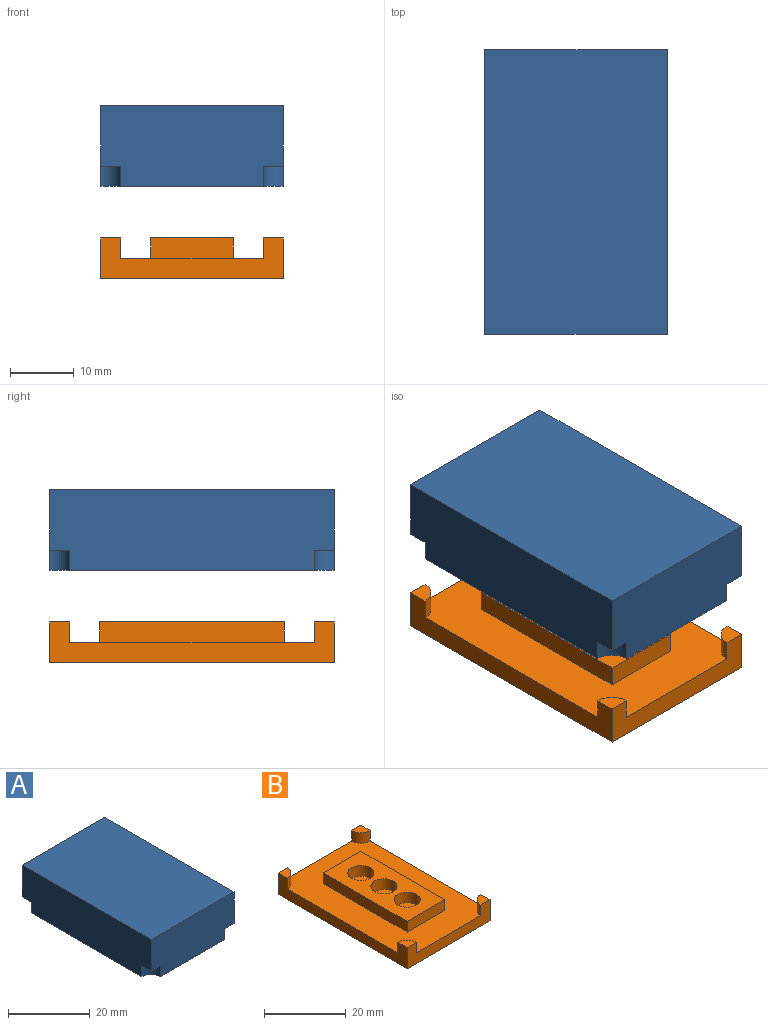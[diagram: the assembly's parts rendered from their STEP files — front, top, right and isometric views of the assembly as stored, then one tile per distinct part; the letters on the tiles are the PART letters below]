
ASSEMBLY  parts=2 mates=1
PART A: 55 faces, bbox 28.7x44.7x12.7 mm
  f0: plane 44.7x28.7mm, normal (0,0,-1), area 739.2mm2, adj f1,f2,f3,f4,f18,f19,f20,f21
  f1: plane 28.7x12.7mm, normal (0,-1,0), area 344.3mm2, adj f0,f2,f4,f5,f47,f48,f53,f54
  f2: plane 44.7x12.7mm, normal (-1,0,0), area 547.5mm2, adj f0,f1,f3,f5,f51,f52,f53,f54
  f3: plane 28.7x12.7mm, normal (0,1,0), area 344.3mm2, adj f0,f2,f4,f5,f49,f50,f51,f52
  f4: plane 44.7x12.7mm, normal (1,0,0), area 547.5mm2, adj f0,f1,f3,f5,f47,f48,f49,f50
  f5: plane 44.7x28.7mm, normal (0,0,1), area 1282.9mm2, adj f1,f2,f3,f4
  f6: plane 4.4x4.4mm, normal (0,0,-1), area 15.2mm2, adj f31
  f7: cylinder r=2.4mm len=4.8mm, axis (0,0,-1), area 24.1mm2, adj f22,f31
  f8: plane 4.4x4.4mm, normal (0,0,-1), area 15.2mm2, adj f28
  f9: cylinder r=2.4mm len=4.8mm, axis (0,0,-1), area 24.1mm2, adj f22,f28
  f10: plane 4.4x4.4mm, normal (0,0,-1), area 15.2mm2, adj f27
  f11: cylinder r=2.4mm len=4.8mm, axis (0,0,-1), area 24.1mm2, adj f22,f27
  f12: plane 4.4x4.4mm, normal (0,0,-1), area 15.2mm2, adj f26
  f13: cylinder r=2.4mm len=4.8mm, axis (0,0,-1), area 24.1mm2, adj f22,f26
  f14: plane 4.4x4.4mm, normal (0,0,-1), area 15.2mm2, adj f30
  f15: cylinder r=2.4mm len=4.8mm, axis (0,0,-1), area 24.1mm2, adj f22,f30
  f16: plane 4.4x4.4mm, normal (0,0,-1), area 15.2mm2, adj f29
  f17: cylinder r=2.4mm len=4.8mm, axis (0,0,-1), area 24.1mm2, adj f22,f29
  f18: plane 31.9x9.55mm, normal (1,0,0), area 304.6mm2, adj f0,f36,f41,f42
  f19: plane 15.9x9.55mm, normal (0,1,0), area 151.8mm2, adj f0,f34,f35,f36
  f20: plane 31.9x9.55mm, normal (-1,0,0), area 304.6mm2, adj f0,f34,f39,f40
  f21: plane 15.9x9.55mm, normal (0,-1,0), area 151.8mm2, adj f0,f39,f42,f45
  f22: plane 31.9x15.9mm, normal (0,0,-1), area 362.4mm2, adj f7,f9,f11,f13,f15,f17,f23,f24
  f23: cylinder r=2.4mm len=4.8mm, axis (0,0,-1), area 24.1mm2, adj f22,f33
  f24: cylinder r=2.4mm len=4.8mm, axis (0,0,-1), area 24.1mm2, adj f22,f32
  f25: plane 4.4x4.4mm, normal (0,0,-1), area 15.2mm2, adj f32
  f26: torus R=2.2mm, axis (0,0,1), area 4.6mm2, adj f12,f13
  f27: torus R=2.2mm, axis (0,0,1), area 4.6mm2, adj f10,f11
  f28: torus R=2.2mm, axis (0,0,1), area 4.6mm2, adj f8,f9
  f29: torus R=2.2mm, axis (0,0,1), area 4.6mm2, adj f16,f17
  f30: torus R=2.2mm, axis (0,0,1), area 4.6mm2, adj f14,f15
  f31: torus R=2.2mm, axis (0,0,1), area 4.6mm2, adj f6,f7
  f32: torus R=2.2mm, axis (0,0,1), area 4.6mm2, adj f24,f25
  f33: torus R=2.2mm, axis (0,0,1), area 4.6mm2, adj f23,f46
  f34: cylinder r=0.05mm len=9.55mm, axis (0,0,-1), area 0.8mm2, adj f0,f19,f20,f37
  f35: cylinder r=0.05mm len=15.9mm, axis (1,0,0), area 1.2mm2, adj f19,f22,f37,f38
  f36: cylinder r=0.05mm len=9.55mm, axis (0,0,-1), area 0.8mm2, adj f0,f18,f19,f38
  f37: sphere r=0.05mm, area 0mm2, adj f34,f35,f40
  f38: sphere r=0.05mm, area 0mm2, adj f35,f36,f41
  f39: cylinder r=0.05mm len=9.55mm, axis (0,0,-1), area 0.8mm2, adj f0,f20,f21,f43
  f40: cylinder r=0.05mm len=31.9mm, axis (0,1,0), area 2.5mm2, adj f20,f22,f37,f43
  f41: cylinder r=0.05mm len=31.9mm, axis (0,-1,0), area 2.5mm2, adj f18,f22,f38,f44
  f42: cylinder r=0.05mm len=9.55mm, axis (0,0,-1), area 0.8mm2, adj f0,f18,f21,f44
  f43: sphere r=0.05mm, area 0mm2, adj f39,f40,f45
  f44: sphere r=0.05mm, area 0mm2, adj f41,f42,f45
  f45: cylinder r=0.05mm len=15.9mm, axis (-1,0,0), area 1.2mm2, adj f21,f22,f43,f44
  f46: plane 4.4x4.4mm, normal (0,0,-1), area 15.2mm2, adj f33
  f47: cylinder r=3.17mm len=3.18mm, axis (0,0,-1), area 15.8mm2, adj f0,f1,f4,f48
  f48: plane 3.18x3.18mm, normal (0,0,-1), area 7.9mm2, adj f1,f4,f47
  f49: cylinder r=3.17mm len=3.18mm, axis (0,0,-1), area 15.8mm2, adj f0,f3,f4,f50
  f50: plane 3.18x3.18mm, normal (0,0,-1), area 7.9mm2, adj f3,f4,f49
  f51: cylinder r=3.17mm len=3.18mm, axis (0,0,-1), area 15.8mm2, adj f0,f2,f3,f52
  f52: plane 3.18x3.18mm, normal (0,0,-1), area 7.9mm2, adj f2,f3,f51
  f53: cylinder r=3.17mm len=3.18mm, axis (0,0,-1), area 15.8mm2, adj f0,f1,f2,f54
  f54: plane 3.18x3.18mm, normal (0,0,-1), area 7.9mm2, adj f1,f2,f53
PART B: 25 faces, bbox 28.7x44.7x6.4 mm
  f0: cylinder r=3.2mm len=6.4mm, axis (0,0,-1), area 64.3mm2, adj f6,f9
  f1: cylinder r=3.2mm len=6.4mm, axis (0,0,-1), area 64.3mm2, adj f6,f10
  f2: plane 13x3.2mm, normal (0,1,0), area 41.6mm2, adj f3,f5,f6,f11
  f3: plane 29x3.2mm, normal (-1,0,0), area 92.8mm2, adj f2,f4,f6,f11
  f4: plane 13x3.2mm, normal (0,-1,0), area 41.6mm2, adj f3,f5,f6,f11
  f5: plane 29x3.2mm, normal (1,0,0), area 92.8mm2, adj f2,f4,f6,f11
  f6: plane 29x13mm, normal (0,0,1), area 280.5mm2, adj f0,f1,f2,f3,f4,f5,f7
  f7: cylinder r=3.2mm len=6.4mm, axis (0,0,-1), area 64.3mm2, adj f6,f8
  f8: plane 6.4x6.4mm, normal (0,0,1), area 32.2mm2, adj f7
  f9: plane 6.4x6.4mm, normal (0,0,1), area 32.2mm2, adj f0
  f10: plane 6.4x6.4mm, normal (0,0,1), area 32.2mm2, adj f1
  f11: plane 44.7x28.7mm, normal (0,0,1), area 874.2mm2, adj f2,f3,f4,f5,f12,f13,f14,f15
  f12: plane 28.7x6.35mm, normal (0,-1,0), area 111.3mm2, adj f11,f13,f15,f16,f18,f19,f22,f23
  f13: plane 44.7x6.35mm, normal (-1,0,0), area 162.1mm2, adj f11,f12,f14,f16,f19,f20,f21,f22
  f14: plane 28.7x6.35mm, normal (0,1,0), area 111.3mm2, adj f11,f13,f15,f16,f17,f20,f21,f24
  f15: plane 44.7x6.35mm, normal (1,0,0), area 162.1mm2, adj f11,f12,f14,f16,f17,f18,f23,f24
  f16: plane 44.7x28.7mm, normal (0,0,-1), area 1282.9mm2, adj f12,f13,f14,f15
  f17: plane 3.18x3.18mm, normal (0,0,1), area 7.9mm2, adj f14,f15,f24
  f18: plane 3.18x3.18mm, normal (0,0,1), area 7.9mm2, adj f12,f15,f23
  f19: plane 3.18x3.18mm, normal (0,0,1), area 7.9mm2, adj f12,f13,f22
  f20: plane 3.18x3.18mm, normal (0,0,1), area 7.9mm2, adj f13,f14,f21
  f21: cylinder r=3.17mm len=3.18mm, axis (0,0,1), area 15.8mm2, adj f11,f13,f14,f20
  f22: cylinder r=3.17mm len=3.18mm, axis (0,0,1), area 15.8mm2, adj f11,f12,f13,f19
  f23: cylinder r=3.17mm len=3.18mm, axis (0,0,1), area 15.8mm2, adj f11,f12,f15,f18
  f24: cylinder r=3.17mm len=3.18mm, axis (0,0,1), area 15.8mm2, adj f11,f14,f15,f17
PLACE A rot(axis=(-0.27,0.03,0.96),0deg) t=(-46.5,-5.91,28.45)mm
PLACE B t=(-46.5,-5.91,17.18)mm
MATE slider B.f24 <-> A.f49  axis (0,0,1) through (-24.15,32.44,12.37)mm
